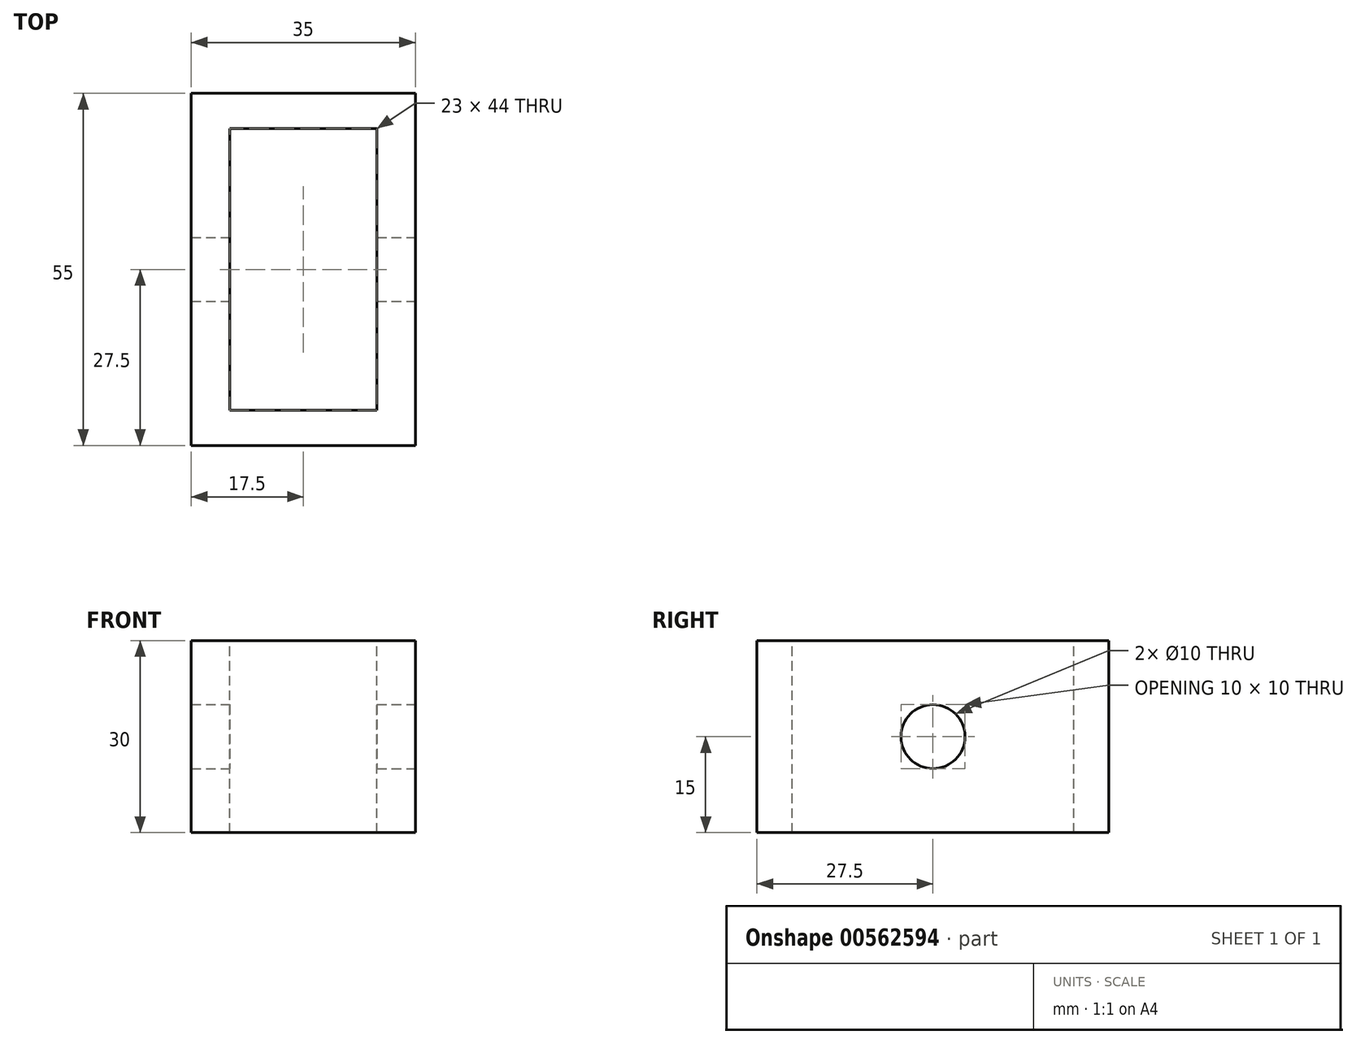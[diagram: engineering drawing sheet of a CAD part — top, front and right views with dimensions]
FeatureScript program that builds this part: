
annotation { "Feature Type Name" : "Feature", "Feature Type Description" : "" }
export const myFeature = defineFeature(function(context is Context, id is Id, definition is map)
    precondition{}
    {
        {
            var Q0;
            Q0=qCreatedBy(makeId("Top.planeOp"),FACE);
            var sketch = newSketch(context, id + "F0", { "sketchPlane" : qUnion([Q0])});
            skLineSegment(sketch, "E0.bottom", {"start": v(-17.5, 27.5) * mm, "end": v(17.5, 27.5) * mm});
            skLineSegment(sketch, "E0.top", {"start": v(-17.5, -27.5) * mm, "end": v(17.5, -27.5) * mm});
            skLineSegment(sketch, "E0.left", {"start": v(-17.5, 27.5) * mm, "end": v(-17.5, -27.5) * mm});
            skLineSegment(sketch, "E0.right", {"start": v(17.5, 27.5) * mm, "end": v(17.5, -27.5) * mm});
            skPoint(sketch, "E0.middle", {"position": v(0, 0) * mm});
            skSolve(sketch);
        }
        {
            var Q0;
            Q0=makeQuery(id+"F0.imprint","IMPRINT",FACE,{"disambiguationData":[TD([[makeQuery(id+"F0.imprint","IMPRINT",EDGE,{"derivedFrom":sQuery(id+"F0.wireOp",EDGE,"E0.bottom")}),-1.0]])]});
            extrude(context, id + "F1", {"entities" : qUnion([Q0]), "depth" : 30 * mm, "offsetDistance" : 25 * mm});
        }
        {
            var Q0;
            Q0=makeQuery(id+"F1.opExtrude","CAP_FACE",FACE,{"disambiguationData":[OSD([sQuery(id+"F0.wireOp",EDGE,"E0.bottom"),sQuery(id+"F0.wireOp",EDGE,"E0.top"),sQuery(id+"F0.wireOp",EDGE,"E0.left"),sQuery(id+"F0.wireOp",EDGE,"E0.right")])],"isStart":false});
            var sketch = newSketch(context, id + "F2", { "sketchPlane" : qUnion([Q0])});
            skSolve(sketch);
        }
        {
            var Q0;
            Q0=makeQuery(id+"F2.imprint","IMPRINT",FACE,{"disambiguationData":[TD([[makeQuery(id+"F2.imprint","IMPRINT",EDGE,{"derivedFrom":makeQuery(id+"F1.opExtrude","CAP_EDGE",EDGE,{"disambiguationData":[OSD([sQuery(id+"F0.wireOp",EDGE,"E0.bottom")])],"isStart":false})}),-1.0]])]});
            var sketch = newSketch(context, id + "F3", { "sketchPlane" : qUnion([Q0])});
            skLineSegment(sketch, "E1.bottom", {"start": v(-11.5, 22) * mm, "end": v(11.5, 22) * mm});
            skLineSegment(sketch, "E1.top", {"start": v(-11.5, -22) * mm, "end": v(11.5, -22) * mm});
            skLineSegment(sketch, "E1.left", {"start": v(-11.5, 22) * mm, "end": v(-11.5, -22) * mm});
            skLineSegment(sketch, "E1.right", {"start": v(11.5, 22) * mm, "end": v(11.5, -22) * mm});
            skPoint(sketch, "E1.middle", {"position": v(0, 0) * mm});
            skSolve(sketch);
        }
        {
            var Q0;
            Q0=makeQuery(id+"F3.imprint","IMPRINT",FACE,{"disambiguationData":[TD([[makeQuery(id+"F3.imprint","IMPRINT",EDGE,{"derivedFrom":sQuery(id+"F3.wireOp",EDGE,"E1.bottom")}),-1.0]])]});
            extrude(context, id + "F4", {"entities" : qUnion([Q0]), "operationType" : NewBodyOperationType.REMOVE, "oppositeDirection" : true, "depth" : 40 * mm, "offsetDistance" : 25 * mm});
        }
        {
            var Q0;
            Q0=makeQuery(id+"F1.opExtrude","SWEPT_FACE",FACE,{"disambiguationData":[OSD([sQuery(id+"F0.wireOp",EDGE,"E0.right")])]});
            var sketch = newSketch(context, id + "F5", { "sketchPlane" : qUnion([Q0])});
            skLineSegment(sketch, "E2", {"start": v(0, 30) * mm, "end": v(0, 0) * mm});
            skLineSegment(sketch, "E3", {"start": v(-27.5, 15) * mm, "end": v(27.5, 15) * mm});
            skPoint(sketch, "E4", {"position": v(0, 15) * mm});
            skSolve(sketch);
        }
        {
            var Q0;
            Q0=sQuery(id+"F5.wireOp",VERTEX,"E4");
            var Q1;
            Q1=makeQuery(id+"F1.opExtrude","SWEPT_BODY",BODY,{"disambiguationData":[OSD([sQuery(id+"F0.wireOp",EDGE,"E0.bottom"),sQuery(id+"F0.wireOp",EDGE,"E0.top"),sQuery(id+"F0.wireOp",EDGE,"E0.left"),sQuery(id+"F0.wireOp",EDGE,"E0.right")])]});
            hole(context, id + "F6", {"style" : HoleStyle.SIMPLE, "endStyle" : HoleEndStyle.THROUGH, "holeDiameter" : 10 * mm, "isTappedThrough" : true, "tappedDepth" : 12 * mm, "tapClearance" : 3, "locations" : qUnion([Q0]), "scope" : qUnion([Q1])});
        }
    });
